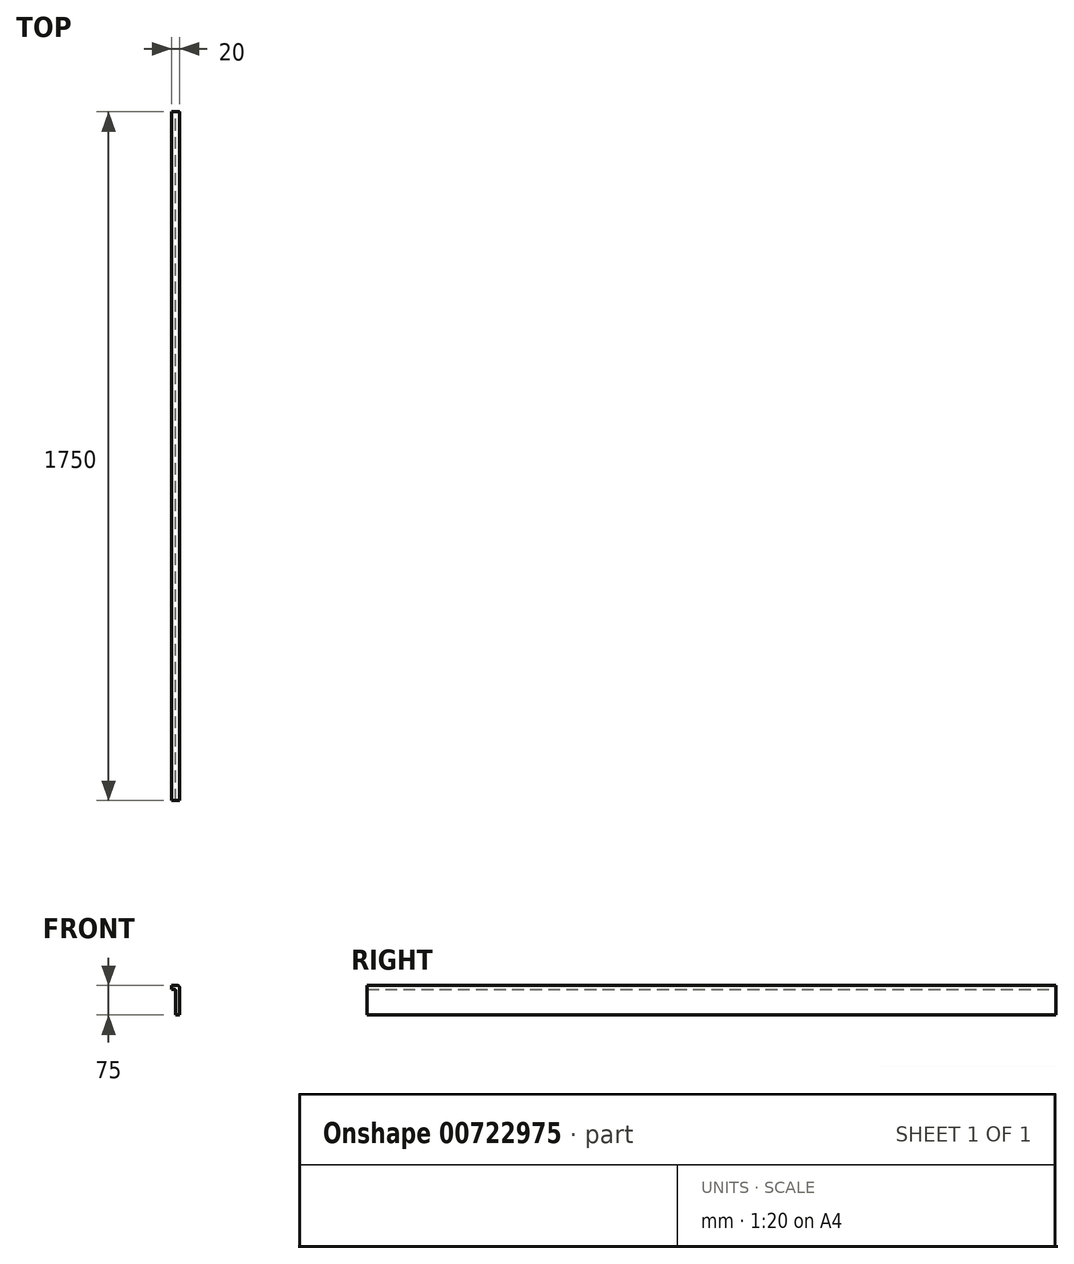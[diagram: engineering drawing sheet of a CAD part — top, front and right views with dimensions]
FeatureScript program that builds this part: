
annotation { "Feature Type Name" : "Feature", "Feature Type Description" : "" }
export const myFeature = defineFeature(function(context is Context, id is Id, definition is map)
    precondition{}
    {
        {
            var Q0;
            Q0=qCreatedBy(makeId("Front.planeOp"),FACE);
            var sketch = newSketch(context, id + "F0", { "sketchPlane" : qUnion([Q0])});
            skLineSegment(sketch, "E0", {"start": v(-20, 0) * mm, "end": v(0, 0) * mm});
            skLineSegment(sketch, "E1", {"start": v(0, 0) * mm, "end": v(0, -75) * mm});
            skLineSegment(sketch, "E2", {"start": v(-20, 0) * mm, "end": v(-20, -10) * mm});
            skLineSegment(sketch, "E3", {"start": v(-20, -10) * mm, "end": v(-10, -10) * mm});
            skLineSegment(sketch, "E4", {"start": v(-10, -10) * mm, "end": v(-10, -75) * mm});
            skLineSegment(sketch, "E5", {"start": v(-10, -75) * mm, "end": v(0, -75) * mm});
            skSolve(sketch);
        }
        {
            var Q0;
            Q0=makeQuery(id+"F0.imprint","IMPRINT",FACE,{"disambiguationData":[TD([[makeQuery(id+"F0.imprint","IMPRINT",EDGE,{"derivedFrom":sQuery(id+"F0.wireOp",EDGE,"E0")}),-1.0]])]});
            extrude(context, id + "F1", {"entities" : qUnion([Q0]), "depth" : 1750 * mm, "offsetDistance" : 25 * mm});
        }
        {
            var Q0;
            Q0=makeQuery(id+"F1.opExtrude","SWEPT_EDGE",EDGE,{"disambiguationData":[OSD([sQuery(id+"F0.wireOp",EDGE,"E0"),sQuery(id+"F0.wireOp",EDGE,"E1")])]});
            fillet(context, id + "F2", {"entities" : qUnion([Q0]), "radius" : 4 * mm, "tangentPropagation" : true, "allowEdgeOverflow" : false});
        }
        {
            var Q0;
            Q0=makeQuery(id+"F1.opExtrude","SWEPT_EDGE",EDGE,{"disambiguationData":[OSD([sQuery(id+"F0.wireOp",EDGE,"E3"),sQuery(id+"F0.wireOp",EDGE,"E4")])]});
            fillet(context, id + "F3", {"entities" : qUnion([Q0]), "radius" : 2 * mm, "tangentPropagation" : true, "allowEdgeOverflow" : false});
        }
    });
